# Revit family: 307_606ee224e8d048cdbafcc5596280ca
name_source: partatom
category: Pipe Accessories
units: mm (PartAtom-declared; Revit-internal decimal feet)

## family parameters
Always vertical = Yes
Cut with Voids When Loaded = No
Part Type = Breaks Into
Round Connector Dimension = Use Diameter
Shared = No
Work Plane-Based = No

## types (4) — shared parameters
B1 = 2 mm  [stored 0.00656168 ft]
B11 = 13 mm  [stored 0.0426509 ft]
B11__ve = -13 mm  [stored -0.0426509 ft]
B1__ve = -2 mm  [stored -0.00656168 ft]
CenSd_NR1_6 = 15 mm  [stored 0.0492126 ft]
CenSd_NR_6 = 10 mm  [stored 0.0328084 ft]
Description = Flanged dirt separator with magnetic inserts, drain valve
EEE = 8 mm  [stored 0.0262467 ft]
EEE__ve = -8 mm  [stored -0.0262467 ft]
HD2 = 5 mm  [stored 0.0164042 ft]
L2D = 511 mm
L2D_Min = 3048 mm
Manufacturer = FAR
NR = 11 mm
NR1 = 18 mm
QmdConnectorList = 301;D;302;D
R2 = 13 mm  [stored 0.0426509 ft]
RH = 12 mm  [stored 0.0393701 ft]
W2D = 100 mm  [stored 0.328084 ft]
magiPartTypeId = 307
magiProductFamilyId = 606ee224e8d048cdbafcc5596280ca

## per-type parameters (varying)
| type | A | D | D12 | DM1 | DM2 | G | G4 | HC | HCD2 | HE | HE1 | HT | L1 | LL | LM | R | RC | magiProductId |
| 2241 100 | 497 mm | 100 mm | 75 mm  [stored 0.246063 ft] | 60 mm  [stored 0.19685 ft] | 52 mm  [stored 0.170604 ft] | 157 mm | 63 mm | 46 mm | 65 mm  [stored 0.213255 ft] | Yes | No | 161 mm  [stored 0.528215 ft] | 26 mm | 256 mm | 430 mm | 50 mm  [stored 0.164042 ft] | 36 mm | 26b094769de143c8bc89c65ae879d0 |
| 2241 50 | 387 mm | 50 mm | 50 mm  [stored 0.164042 ft] | 30 mm  [stored 0.0984252 ft] | 32 mm  [stored 0.104987 ft] | 104 mm | 42 mm | 28 mm | 40 mm  [stored 0.131234 ft] | No | Yes | 131 mm | 17 mm | 172 mm  [stored 0.564304 ft] | 280 mm | 25 mm  [stored 0.082021 ft] | 30 mm  [stored 0.0984252 ft] | 34147461daea42d1903f0917082513 |
| 2241 65 | 387 mm | 65 mm | 50 mm  [stored 0.164042 ft] | 39 mm  [stored 0.127953 ft] | 32 mm  [stored 0.104987 ft] | 104 mm | 42 mm | 28 mm | 40 mm  [stored 0.131234 ft] | Yes | No | 131 mm | 17 mm | 172 mm  [stored 0.564304 ft] | 280 mm | 33 mm | 30 mm  [stored 0.0984252 ft] | 32a0813e50204472a5a33c8245fb49 |
| 2241 80 | 497 mm | 80 mm | 75 mm  [stored 0.246063 ft] | 48 mm  [stored 0.15748 ft] | 48 mm  [stored 0.15748 ft] | 157 mm | 63 mm | 42 mm | 60 mm  [stored 0.19685 ft] | Yes | No | 161 mm  [stored 0.528215 ft] | 26 mm | 256 mm | 430 mm | 40 mm  [stored 0.131234 ft] | 36 mm | f39bac49a72645a088c367fdd8a140 |

note: column(s) folded — value = type name in every type: MC Product Code

note: [stored X ft] marks values corroborated as IEEE doubles in the binary element streams (Revit-internal decimal feet)

## geometry (parser evidence)
native form markers: Sweep x3
no freeform markers — native parametric forms only
